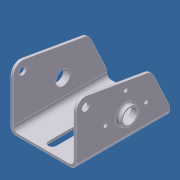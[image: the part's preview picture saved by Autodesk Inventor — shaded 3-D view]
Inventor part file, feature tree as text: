
AUTODESK INVENTOR PART (.ipt)
format: ipt  version: unknown  size: 326,144 bytes
history: native  units: in
note: dims shown in document units (in); Inventor stores cm internally (conversion verified against a paired STEP export)
features: extrude x7, sketch x7, fillet x5, plane x1, mirror x1, reference x1
ambient origin geometry x8: Origin, YZ Plane, XZ Plane, XY Plane, X Axis, Y Axis, Z Axis, Center Point
bodies: Solid1 (feature_tree)
feature tree (22):
  extrude  "Extrusion1"  Depth=0.12in
  fillet  "Fillet1"  Radius=0.12in
  extrude  "Extrusion2"  Depth=3.095in
  fillet  "Fillet2"  [1 undecoded]
  extrude  "Extrusion3"  Depth=0.5in
  fillet  "Fillet3"  Radius=0.375in
  fillet  "Fillet4"  Radius=4.872in
  extrude  "Extrusion4"  Depth=0.25in
  extrude  "Extrusion5"  Depth=0.4466in
  sketch  "Sketch6"  dims[d17=4.872in d18=0.0in d19=0.5in d20=0.5in]
  plane  "Work Plane1"
  mirror  "Mirror1"
  extrude  "Extrusion6"  Depth=0.5in
  fillet  "Fillet5"  Radius=0.5in
  extrude  "Extrusion7"  Depth=0.425in
  sketch  "Sketch1"  dims[d0=3.4in d1=0.12in d2=0.12in]
  sketch  "Sketch2"  dims[d3=0.12in d4=3.095in d5=0.0in]
  sketch  "Sketch3"  dims[d6=4.872in d7=0.0in d8=0.5in d9=0.375in d10=4.872in d11=0.0in]
  sketch  "Sketch4"  dims[d12=0.25in d13=0.25in]
  sketch  "Sketch5"  dims[d15=0.8589in d16=0.4466in]
  sketch  "Sketch7"  dims[d21=0.425in d22=0.425in d23=1.0in d24=0.4625in d25=0.425in d26=0.4253in d27=0.4625in d28=1.217in d29=1.217in d30=1.217in d31=4.872in d32=0.0in d33=0.75in d36=0.9in d37=1.24in d38=2.5in d39=0.215in d40=0.0in d41=0.215in d42=0.0in d43=0.1in d44=1.0in d45=0.0in]
  reference  "Reference1"
note: 1 required parameter value undecoded (feature->parameter linkage not recoverable at this tier; creation-order binding heuristic only, values carry confidence <= 0.55)
